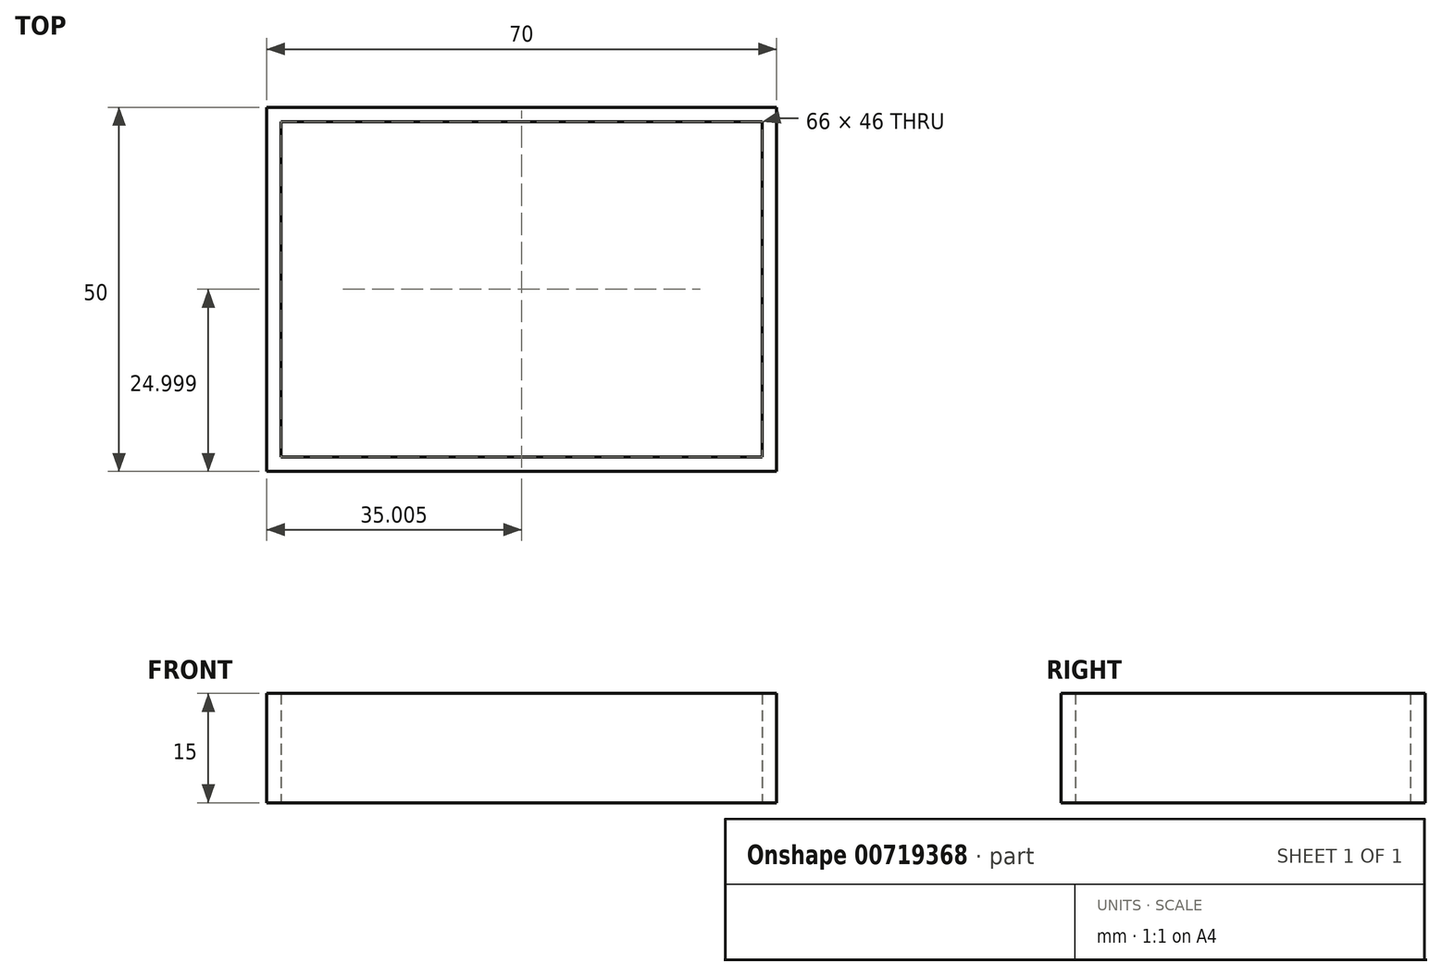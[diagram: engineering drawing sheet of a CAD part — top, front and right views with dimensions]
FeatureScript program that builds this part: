
annotation { "Feature Type Name" : "Feature", "Feature Type Description" : "" }
export const myFeature = defineFeature(function(context is Context, id is Id, definition is map)
    precondition{}
    {
        {
            var Q0;
            Q0=qCreatedBy(makeId("Top.planeOp"),FACE);
            var sketch = newSketch(context, id + "F0", { "sketchPlane" : qUnion([Q0])});
            skLineSegment(sketch, "E0.bottom", {"start": v(-18, 22.7) * mm, "end": v(52, 22.7) * mm});
            skLineSegment(sketch, "E0.top", {"start": v(-18, -27.3) * mm, "end": v(52, -27.3) * mm});
            skLineSegment(sketch, "E0.left", {"start": v(-18, 22.7) * mm, "end": v(-18, -27.3) * mm});
            skLineSegment(sketch, "E0.right", {"start": v(52, 22.7) * mm, "end": v(52, -27.3) * mm});
            skLineSegment(sketch, "E1.0", {"start": v(-16, 20.7) * mm, "end": v(50, 20.7) * mm});
            skLineSegment(sketch, "E1.1", {"start": v(-16, 20.7) * mm, "end": v(-16, -25.3) * mm});
            skLineSegment(sketch, "E1.2", {"start": v(-16, -25.3) * mm, "end": v(50, -25.3) * mm});
            skLineSegment(sketch, "E1.3", {"start": v(50, 20.7) * mm, "end": v(50, -25.3) * mm});
            skSolve(sketch);
        }
        {
            var Q0;
            Q0 = qSketchRegion(id + "F0", true);
            extrude(context, id + "F1", {"entities" : qUnion([Q0]), "depth" : 15 * mm, "offsetDistance" : 25.4 * mm});
        }
    });
